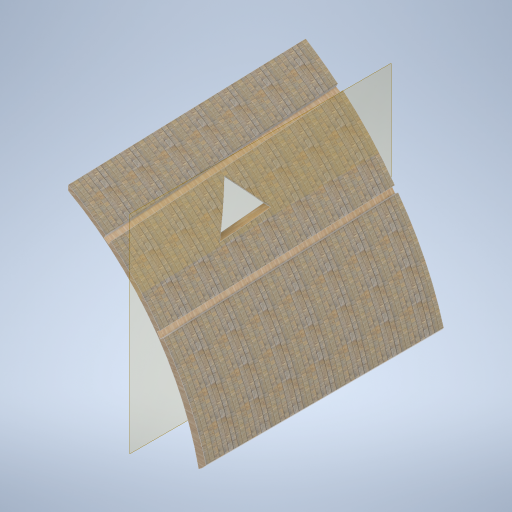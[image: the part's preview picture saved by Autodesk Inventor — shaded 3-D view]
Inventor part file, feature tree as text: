
AUTODESK INVENTOR PART (.ipt)
format: ipt  version: 2024.2 (Build 282272000, 272)  size: 508,928 bytes
history: native  units: mm
features: sketch x3, plane x3, loft x1, extrude x1
ambient origin geometry x8: Origin, YZ Plane, XZ Plane, XY Plane, X Axis, Y Axis, Z Axis, Center Point
bodies: Solid1 (feature_tree)
feature tree (8):
  sketch  "Sketch1"  dims[d5=0.0mm d6=-8101.0mm d7=800.0mm]
  plane  "Work Plane2"
  loft  "Loft1"
  plane  "Work Plane3"
  extrude  "Extrusion1"  TaperAngle=0.0deg  [1 undecoded]
  plane  "Work Plane1"
  sketch  "Sketch2"  dims[d8=0.0mm d9=90.0deg d10=0.0mm d11=90.0deg]
  sketch  "Sketch3"  dims[d12=2600.0mm d13=0.0mm d14=0.0mm d15=500.0mm d16=0.872665mm]
note: 1 required parameter value undecoded (feature->parameter linkage not recoverable at this tier; creation-order binding heuristic only, values carry confidence <= 0.55)
